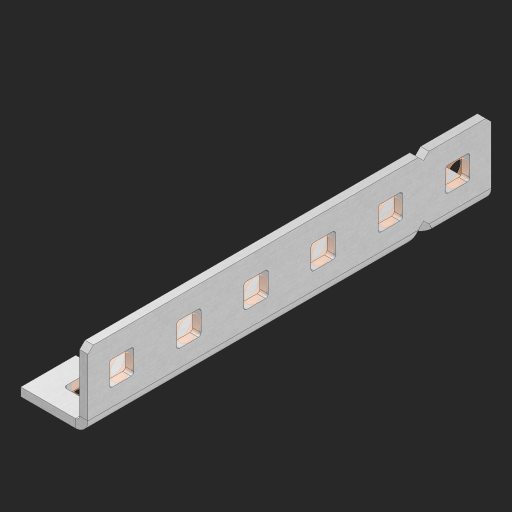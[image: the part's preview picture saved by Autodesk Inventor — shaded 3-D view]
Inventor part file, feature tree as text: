
AUTODESK INVENTOR PART (.ipt)
format: ipt  version: 2023 (Build 270158000, 158)  size: 554,496 bytes
history: native  units: in
note: dims shown in document units (in); Inventor stores cm internally (conversion verified against a paired STEP export)
features: other x166, extrude x16, sheet_metal_op x11, sketch x10, pattern_linear x2, mirror x1, chamfer x1
ambient origin geometry x8: Origin, YZ Plane, XZ Plane, XY Plane, X Axis, Y Axis, Z Axis, Center Point
bodies: Solid1 (feature_tree), Body (feature_tree)
feature tree (207):
  other  "Alu Half C 1x2x1x6"
  other  "Table"
  other  "Alu C 1x2x1x35"
  other  "Alu C 1x2x1x34"
  other  "Alu C 1x2x1x33"
  other  "Alu C 1x2x1x32"
  other  "Alu C 1x2x1x31"
  other  "Alu C 1x2x1x30"
  other  "Alu C 1x2x1x29"
  other  "Alu C 1x2x1x28"
  other  "Alu C 1x2x1x27"
  other  "Alu C 1x2x1x26"
  other  "Alu C 1x2x1x25"
  other  "Alu C 1x2x1x24"
  other  "Alu C 1x2x1x23"
  other  "Alu C 1x2x1x22"
  other  "Alu C 1x2x1x21"
  other  "Alu C 1x2x1x20"
  other  "Alu C 1x2x1x19"
  other  "Alu C 1x2x1x18"
  other  "Alu C 1x2x1x17"
  other  "Alu C 1x2x1x16"
  other  "Alu C 1x2x1x15"
  other  "Alu C 1x2x1x14"
  other  "Alu C 1x2x1x13"
  other  "Alu C 1x2x1x12"
  other  "Alu C 1x2x1x11"
  other  "Alu C 1x2x1x10"
  other  "Alu C 1x2x1x9"
  other  "Alu C 1x2x1x8"
  other  "Alu C 1x2x1x7"
  other  "Alu C 1x2x1x6"
  other  "Alu C 1x2x1x5"
  other  "Alu C 1x2x1x4"
  other  "Alu C 1x2x1x3"
  other  "Alu C 1x2x1x2"
  other  "Alu C 1x2x1x1"
  other  "Steel C 1x2x1x35"
  other  "Steel C 1x2x1x34"
  other  "Steel C 1x2x1x33"
  other  "Steel C 1x2x1x32"
  other  "Steel C 1x2x1x31"
  other  "Steel C 1x2x1x30"
  other  "Steel C 1x2x1x29"
  other  "Steel C 1x2x1x28"
  other  "Steel C 1x2x1x27"
  other  "Steel C 1x2x1x26"
  other  "Steel C 1x2x1x25"
  other  "Steel C 1x2x1x24"
  other  "Steel C 1x2x1x23"
  other  "Steel C 1x2x1x22"
  other  "Steel C 1x2x1x21"
  other  "Steel C 1x2x1x20"
  other  "Steel C 1x2x1x19"
  other  "Steel C 1x2x1x18"
  other  "Steel C 1x2x1x17"
  other  "Steel C 1x2x1x16"
  other  "Steel C 1x2x1x15"
  other  "Steel C 1x2x1x14"
  other  "Steel C 1x2x1x13"
  other  "Steel C 1x2x1x12"
  other  "Steel C 1x2x1x11"
  other  "Steel C 1x2x1x10"
  other  "Steel C 1x2x1x9"
  other  "Steel C 1x2x1x8"
  other  "Steel C 1x2x1x7"
  other  "Steel C 1x2x1x6"
  other  "Steel C 1x2x1x5"
  other  "Steel C 1x2x1x4"
  other  "Steel C 1x2x1x3"
  other  "Steel C 1x2x1x2"
  other  "Steel C 1x2x1x1"
  other  "Alu Half C 1x2x1x35"
  other  "Alu Half C 1x2x1x34"
  other  "Alu Half C 1x2x1x33"
  other  "Alu Half C 1x2x1x32"
  other  "Alu Half C 1x2x1x31"
  other  "Alu Half C 1x2x1x30"
  other  "Alu Half C 1x2x1x29"
  other  "Alu Half C 1x2x1x28"
  other  "Alu Half C 1x2x1x27"
  other  "Alu Half C 1x2x1x26"
  other  "Alu Half C 1x2x1x25"
  other  "Alu Half C 1x2x1x24"
  other  "Alu Half C 1x2x1x23"
  other  "Alu Half C 1x2x1x22"
  other  "Alu Half C 1x2x1x21"
  other  "Alu Half C 1x2x1x20"
  other  "Alu Half C 1x2x1x19"
  other  "Alu Half C 1x2x1x18"
  other  "Alu Half C 1x2x1x17"
  other  "Alu Half C 1x2x1x16"
  other  "Alu Half C 1x2x1x15"
  other  "Alu Half C 1x2x1x14"
  other  "Alu Half C 1x2x1x13"
  other  "Alu Half C 1x2x1x12"
  other  "Alu Half C 1x2x1x11"
  other  "Alu Half C 1x2x1x10"
  other  "Alu Half C 1x2x1x9"
  other  "Alu Half C 1x2x1x8"
  other  "Alu Half C 1x2x1x7"
  other  "Alu Half C 1x2x1x5"
  other  "Alu Half C 1x2x1x4"
  other  "Alu Half C 1x2x1x3"
  other  "Alu Half C 1x2x1x2"
  other  "Alu Half C 1x2x1x1"
  other  "Steel Half C 1x2x1x35"
  other  "Steel Half C 1x2x1x34"
  other  "Steel Half C 1x2x1x33"
  other  "Steel Half C 1x2x1x32"
  other  "Steel Half C 1x2x1x31"
  other  "Steel Half C 1x2x1x30"
  other  "Steel Half C 1x2x1x29"
  other  "Steel Half C 1x2x1x28"
  other  "Steel Half C 1x2x1x27"
  other  "Steel Half C 1x2x1x26"
  other  "Steel Half C 1x2x1x25"
  other  "Steel Half C 1x2x1x24"
  other  "Steel Half C 1x2x1x23"
  other  "Steel Half C 1x2x1x22"
  other  "Steel Half C 1x2x1x21"
  other  "Steel Half C 1x2x1x20"
  other  "Steel Half C 1x2x1x19"
  other  "Steel Half C 1x2x1x18"
  other  "Steel Half C 1x2x1x17"
  other  "Steel Half C 1x2x1x16"
  other  "Steel Half C 1x2x1x15"
  other  "Steel Half C 1x2x1x14"
  other  "Steel Half C 1x2x1x13"
  other  "Steel Half C 1x2x1x12"
  other  "Steel Half C 1x2x1x11"
  other  "Steel Half C 1x2x1x10"
  other  "Steel Half C 1x2x1x9"
  other  "Steel Half C 1x2x1x8"
  other  "Steel Half C 1x2x1x7"
  other  "Steel Half C 1x2x1x6"
  other  "Steel Half C 1x2x1x5"
  other  "Steel Half C 1x2x1x4"
  other  "Steel Half C 1x2x1x3"
  other  "Steel Half C 1x2x1x2"
  other  "Steel Half C 1x2x1x1"
  sheet_metal_op  "Flanges"
  other  "Flange Pattern Plane"
  other  "Flange Pattern Sketch"
  sheet_metal_op  "Flange Pattern"
  sheet_metal_op  "Body Pattern"
  pattern_linear  "Center Pattern"  Spacing1=0.0625in  [1 undecoded]
  other  "Arc Length"
  mirror  "Notch Mirror"
  pattern_linear  "Notch Pattern"  Spacing1=0.182in  [1 undecoded]
  chamfer  "End Chamfer"
  extrude  "Half Cut"  Depth=0.02in
  sketch  "Sketch1"  dims[d0=1.0in]
  other  "Plate1"
  sketch  "Sketch2"  dims[d1=3.0in]
  other  "Plate2"
  sheet_metal_op  "Bend1"
  sheet_metal_op  "Corner1"
  sketch  "Sketch3"  dims[d2=0.0625in]
  sketch  "Sketch7"  dims[d3=0.0625in]
  other  "Srf1"
  other  "Srf2"
  sketch  "Sketch8"  dims[d4=0.0312in]
  sketch  "Sketch9"  dims[d5=0.125in]
  other  "Srf91"
  sheet_metal_op  "Body Pattern Sketch"
  other  "Srf92"
  sketch  "Sketch13"  dims[d6=0.0625in]
  sketch  "Sketch14"  dims[d7=0.5in d8=90.0deg d9=0.0312in]
  sketch  "Sketch15"  dims[d10=0.25in]
  sketch  "Sketch16"  dims[d11=0.0625in d12=0.0625in d16=0.182in d17=0.02in d18=0.0625in d19=0.0in d20=0.25in d21=0.25in d38=2.3622in d40=0.5in d41=0.3937in d43=1.0in d46=0.172in d47=1.0in d48=0.0in d49=0.182in d50=0.02in d51=0.25in d52=0.25in d53=0.0625in d54=0.0in d55=0.172in d56=1.0in d57=0.0in d58=0.25in d60=2.3622in d62=0.5in d63=0.3937in d65=0.5in d85=0.1473in d86=0.1782in d88=0.04in d89=0.0625in d90=0.0in d91=0.04in d92=0.0491in d95=2.5in d96=0.04in d97=0.25in d98=45.0deg d99=0.25in d100=0.5in d101=0.0in d102=2.497in d106=0.182in d107=0.02in d108=0.5in d109=0.5in d110=0.0625in d111=0.0in d112=0.172in d113=0.5in d114=0.0in d117=0.5in d118=0.5in d119=0.5in]
  other  "Srf786"
  other  "Srf823"
  other  "Srf824"
  other  "Srf825"
  other  "Srf826"
  other  "Srf856"
  other  "Srf857"
  other  "Srf858"
  other  "Srf859"
  other  "Srf889"
  other  "Srf890"
  other  "Srf891"
  other  "Srf892"
  other  "Srf893"
  sheet_metal_op  "Flange Stamp"
  sheet_metal_op  "Flange Circle"
  sheet_metal_op  "Body Stamp"
  sheet_metal_op  "Body Circle"
  other  "Center Stamp"
  other  "Center Circle"
  sheet_metal_op  "Notch"
  extrude  "ExtrusionSrf2"  Depth=0.0625in
  extrude  "ExtrusionSrf92"  TaperAngle=0.0deg  [1 undecoded]
  extrude  "ExtrusionSrf823"  Depth=0.5in
  extrude  "ExtrusionSrf824"  Depth=0.5in
  extrude  "ExtrusionSrf825"  Depth=0.5in
  extrude  "ExtrusionSrf826"  Depth=0.5in
  extrude  "ExtrusionSrf856"  Depth=1.0in TaperAngle=0.0deg
  extrude  "ExtrusionSrf857"  Depth=0.182in
  extrude  "ExtrusionSrf858"  Depth=0.02in
  extrude  "ExtrusionSrf859"  Depth=0.5in
  extrude  "ExtrusionSrf889"  Depth=0.5in
  extrude  "ExtrusionSrf890"  Depth=0.0625in
  extrude  "ExtrusionSrf891"  TaperAngle=0.0deg  [1 undecoded]
  extrude  "ExtrusionSrf892"  Depth=0.5in
  extrude  "ExtrusionSrf893"  Depth=1.0in TaperAngle=0.0deg
note: 4 required parameter values undecoded (feature->parameter linkage not recoverable at this tier; creation-order binding heuristic only, values carry confidence <= 0.55)
